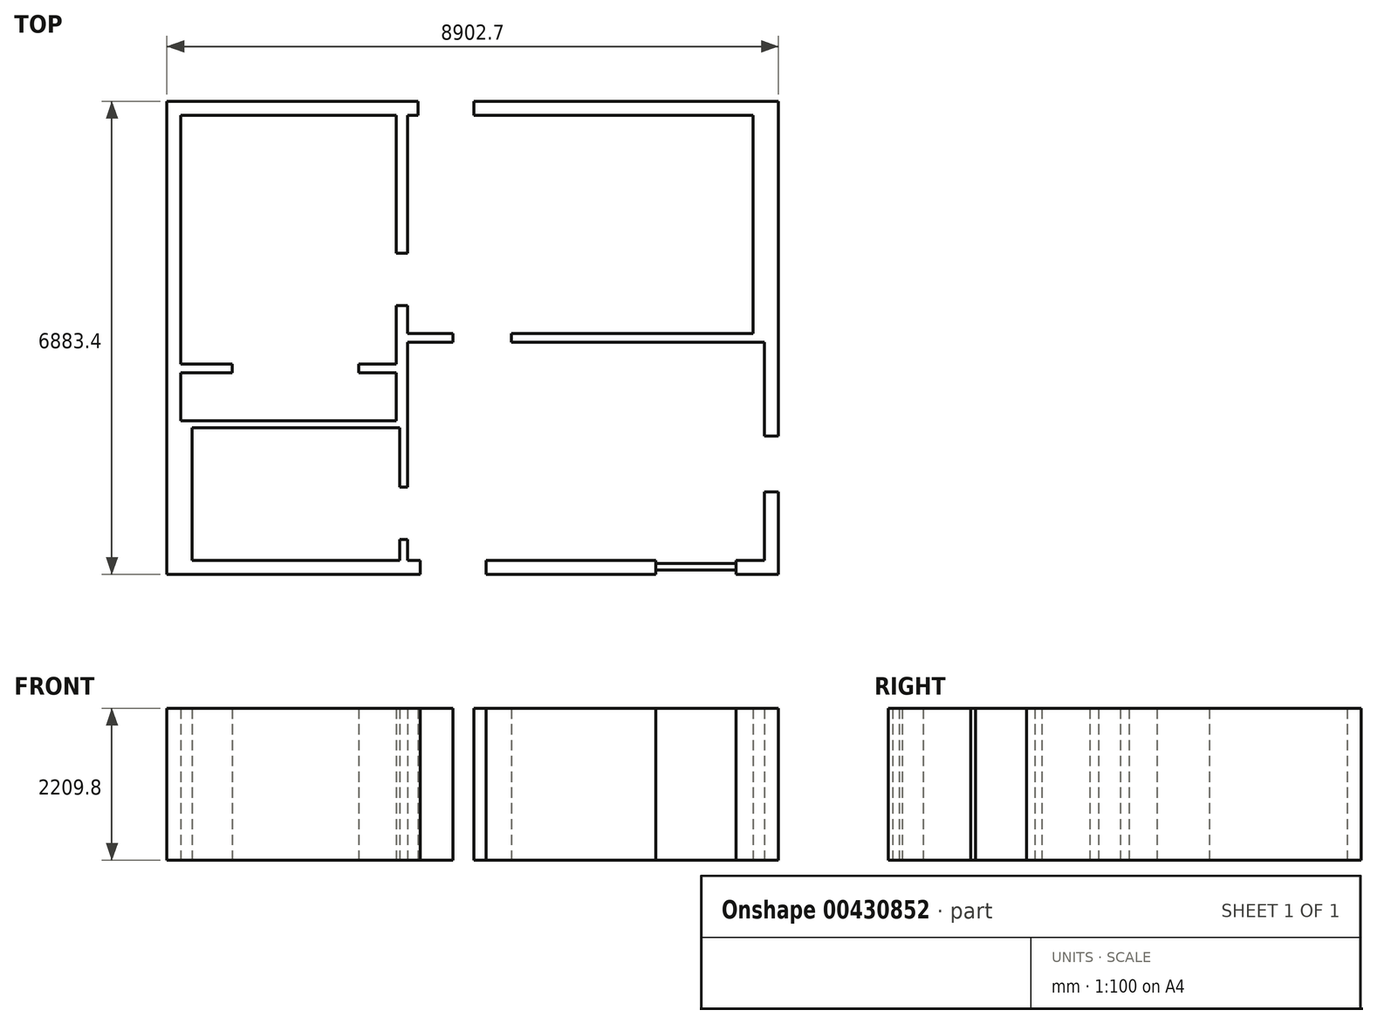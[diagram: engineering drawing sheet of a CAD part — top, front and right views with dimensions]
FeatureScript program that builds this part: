
annotation { "Feature Type Name" : "Feature", "Feature Type Description" : "" }
export const myFeature = defineFeature(function(context is Context, id is Id, definition is map)
    precondition{}
    {
        {
            var Q0;
            Q0=qCreatedBy(makeId("Top.planeOp"),FACE);
            var sketch = newSketch(context, id + "F0", { "sketchPlane" : qUnion([Q0])});
            skLineSegment(sketch, "E0.bottom", {"start": v(-727.6, 2739) * mm, "end": v(-575.2, 2739) * mm});
            skLineSegment(sketch, "E0.top", {"start": v(-727.6, -436) * mm, "end": v(-67.2, -436) * mm});
            skLineSegment(sketch, "E0.left", {"start": v(-727.6, 2739) * mm, "end": v(-727.6, 732.4) * mm});
            skLineSegment(sketch, "E0.right", {"start": v(4301.6, 2739) * mm, "end": v(4301.6, -436) * mm});
            skLineSegment(sketch, "E1.bottom", {"start": v(-727.6, -563) * mm, "end": v(-67.2, -563) * mm});
            skLineSegment(sketch, "E1.top", {"start": v(-727.6, -3738) * mm, "end": v(-546.63, -3738) * mm});
            skLineSegment(sketch, "E1.left", {"start": v(-727.6, -563) * mm, "end": v(-727.6, -2671.2) * mm});
            skLineSegment(sketch, "E1.right", {"start": v(4466.7, -563) * mm, "end": v(4466.7, -1928.26) * mm});
            skLineSegment(sketch, "E2.bottom", {"start": v(-4029.6, -880.5) * mm, "end": v(-3280.3, -880.5) * mm});
            skLineSegment(sketch, "E2.top", {"start": v(-4029.6, 2739) * mm, "end": v(-892.7, 2739) * mm});
            skLineSegment(sketch, "E2.left", {"start": v(-4029.6, -880.5) * mm, "end": v(-4029.6, 2739) * mm});
            skLineSegment(sketch, "E2.right", {"start": v(-892.7, -880.5) * mm, "end": v(-892.7, -29.6) * mm});
            skLineSegment(sketch, "E3.bottom", {"start": v(-3864.5, -1807.6) * mm, "end": v(-841.9, -1807.6) * mm});
            skLineSegment(sketch, "E3.top", {"start": v(-3864.5, -3738) * mm, "end": v(-841.9, -3738) * mm});
            skLineSegment(sketch, "E3.left", {"start": v(-3864.5, -1807.6) * mm, "end": v(-3864.5, -3738) * mm});
            skLineSegment(sketch, "E3.right", {"start": v(-841.9, -1807.6) * mm, "end": v(-841.9, -2671.2) * mm});
            skLineSegment(sketch, "E4", {"start": v(-67.2, -563) * mm, "end": v(-67.2, -436) * mm});
            skLineSegment(sketch, "E5.bottom", {"start": v(-4029.6, -1007.5) * mm, "end": v(-3280.3, -1007.5) * mm});
            skLineSegment(sketch, "E5.top", {"start": v(-4029.6, -1706) * mm, "end": v(-892.7, -1706) * mm});
            skLineSegment(sketch, "E5.left", {"start": v(-4029.6, -1007.5) * mm, "end": v(-4029.6, -1706) * mm});
            skLineSegment(sketch, "E5.right", {"start": v(-892.7, -1007.5) * mm, "end": v(-892.7, -1706) * mm});
            skLineSegment(sketch, "E6", {"start": v(-3280.3, -1007.5) * mm, "end": v(-3280.3, -880.5) * mm});
            skLineSegment(sketch, "E7", {"start": v(-1438.8, -1007.5) * mm, "end": v(-1438.8, -880.5) * mm});
            skLineSegment(sketch, "E8.trimOffspring", {"start": v(-1438.8, -880.5) * mm, "end": v(-892.7, -880.5) * mm});
            skLineSegment(sketch, "E9.trimOffspring", {"start": v(-1438.8, -1007.5) * mm, "end": v(-892.7, -1007.5) * mm});
            skLineSegment(sketch, "E10", {"start": v(783.7, -563) * mm, "end": v(783.7, -436) * mm});
            skLineSegment(sketch, "E11.trimOffspring", {"start": v(783.7, -563) * mm, "end": v(4466.7, -563) * mm});
            skLineSegment(sketch, "E12.trimOffspring", {"start": v(783.7, -436) * mm, "end": v(4301.6, -436) * mm});
            skLineSegment(sketch, "E13", {"start": v(415.4, -3738) * mm, "end": v(415.4, -3941.2) * mm});
            skLineSegment(sketch, "E14", {"start": v(-546.63, -3941.2) * mm, "end": v(-546.63, -3738) * mm});
            skLineSegment(sketch, "E15.bottom", {"start": v(-4232.8, 2942.2) * mm, "end": v(-575.2, 2942.2) * mm});
            skLineSegment(sketch, "E15.top", {"start": v(-4232.8, -3941.2) * mm, "end": v(-546.63, -3941.2) * mm});
            skLineSegment(sketch, "E15.left", {"start": v(-4232.8, 2942.2) * mm, "end": v(-4232.8, -3941.2) * mm});
            skLineSegment(sketch, "E15.right", {"start": v(4669.9, 2942.2) * mm, "end": v(4669.9, -1928.26) * mm});
            skLineSegment(sketch, "E16.trimOffspring", {"start": v(415.4, -3941.2) * mm, "end": v(2885.55, -3941.2) * mm});
            skLineSegment(sketch, "E17.trimOffspring", {"start": v(415.4, -3738) * mm, "end": v(2885.55, -3738) * mm});
            skLineSegment(sketch, "E18", {"start": v(-892.7, -29.6) * mm, "end": v(-727.6, -29.6) * mm});
            skLineSegment(sketch, "E19", {"start": v(-727.6, 732.4) * mm, "end": v(-892.7, 732.4) * mm});
            skLineSegment(sketch, "E20.trimOffspring", {"start": v(-892.7, 732.4) * mm, "end": v(-892.7, 2739) * mm});
            skLineSegment(sketch, "E21.trimOffspring", {"start": v(-727.6, -29.6) * mm, "end": v(-727.6, -436) * mm});
            skLineSegment(sketch, "E22", {"start": v(-841.9, -3433.2) * mm, "end": v(-727.6, -3433.2) * mm});
            skLineSegment(sketch, "E23", {"start": v(-727.6, -2671.2) * mm, "end": v(-841.9, -2671.2) * mm});
            skLineSegment(sketch, "E24.trimOffspring", {"start": v(-727.6, -3433.2) * mm, "end": v(-727.6, -3738) * mm});
            skLineSegment(sketch, "E25.trimOffspring", {"start": v(-841.9, -3433.2) * mm, "end": v(-841.9, -3738) * mm});
            skLineSegment(sketch, "E26", {"start": v(4466.7, -2741.06) * mm, "end": v(4669.9, -2741.06) * mm});
            skLineSegment(sketch, "E27", {"start": v(4669.9, -1928.26) * mm, "end": v(4466.7, -1928.26) * mm});
            skLineSegment(sketch, "E28.trimOffspring", {"start": v(4669.9, -2741.06) * mm, "end": v(4669.9, -3941.2) * mm});
            skLineSegment(sketch, "E29.trimOffspring", {"start": v(4466.7, -2741.06) * mm, "end": v(4466.7, -3738) * mm});
            skLineSegment(sketch, "E30", {"start": v(-575.2, 2739) * mm, "end": v(-575.2, 2942.2) * mm});
            skLineSegment(sketch, "E31", {"start": v(237.6, 2942.2) * mm, "end": v(237.6, 2739) * mm});
            skLineSegment(sketch, "E32.trimOffspring", {"start": v(237.6, 2739) * mm, "end": v(4301.6, 2739) * mm});
            skLineSegment(sketch, "E33.trimOffspring", {"start": v(237.6, 2942.2) * mm, "end": v(4669.9, 2942.2) * mm});
            skLineSegment(sketch, "E34", {"start": v(2885.55, -3941.2) * mm, "end": v(2885.55, -3738) * mm});
            skLineSegment(sketch, "E35", {"start": v(4053.95, -3738) * mm, "end": v(4053.95, -3941.2) * mm});
            skLineSegment(sketch, "E36.trimOffspring", {"start": v(4053.95, -3941.2) * mm, "end": v(4669.9, -3941.2) * mm});
            skLineSegment(sketch, "E37.trimOffspring", {"start": v(4053.95, -3738) * mm, "end": v(4466.7, -3738) * mm});
            skLineSegment(sketch, "E38.bottom", {"start": v(2885.55, -3784.8) * mm, "end": v(4053.95, -3784.8) * mm});
            skLineSegment(sketch, "E38.top", {"start": v(2885.55, -3880.17) * mm, "end": v(4053.95, -3880.17) * mm});
            skLineSegment(sketch, "E38.left", {"start": v(2885.55, -3784.8) * mm, "end": v(2885.55, -3880.17) * mm});
            skLineSegment(sketch, "E38.right", {"start": v(4053.95, -3784.8) * mm, "end": v(4053.95, -3880.17) * mm});
            skSolve(sketch);
        }
        {
            var Q0;
            Q0=makeQuery(id+"F0.imprint","IMPRINT",FACE,{"disambiguationData":[TD([[makeQuery(id+"F0.imprint","IMPRINT",EDGE,{"derivedFrom":sQuery(id+"F0.wireOp",EDGE,"E0.bottom")}),1.0]])]});
            var Q1;
            Q1=makeQuery(id+"F0.imprint","IMPRINT",FACE,{"disambiguationData":[TD([[makeQuery(id+"F0.imprint","IMPRINT",EDGE,{"derivedFrom":sQuery(id+"F0.wireOp",EDGE,"E13")}),1.0]])]});
            var Q2;
            Q2=makeQuery(id+"F0.imprint","IMPRINT",FACE,{"disambiguationData":[TD([[makeQuery(id+"F0.imprint","IMPRINT",EDGE,{"derivedFrom":sQuery(id+"F0.wireOp",EDGE,"E26")}),-1.0]])]});
            var Q3;
            Q3=makeQuery(id+"F0.imprint","IMPRINT",FACE,{"disambiguationData":[TD([[makeQuery(id+"F0.imprint","IMPRINT",EDGE,{"derivedFrom":sQuery(id+"F0.wireOp",EDGE,"E0.right")}),1.0]])]});
            extrude(context, id + "F1", {"entities" : qUnion([Q0, Q1, Q2, Q3]), "depth" : 2209.8 * mm});
        }
        {
            var Q0;
            Q0=makeQuery(id+"F0.imprint","IMPRINT",FACE,{"disambiguationData":[TD([[makeQuery(id+"F0.imprint","IMPRINT",EDGE,{"derivedFrom":sQuery(id+"F0.wireOp",EDGE,"E38.bottom")}),-1.0]])]});
            var Q1;
            Q1=makeQuery(id+"F1.opExtrude","CAP_FACE",FACE,{"disambiguationData":[OSD([sQuery(id+"F0.wireOp",EDGE,"E26"),sQuery(id+"F0.wireOp",EDGE,"E28.trimOffspring"),sQuery(id+"F0.wireOp",EDGE,"E29.trimOffspring"),sQuery(id+"F0.wireOp",EDGE,"E35"),sQuery(id+"F0.wireOp",EDGE,"E36.trimOffspring"),sQuery(id+"F0.wireOp",EDGE,"E37.trimOffspring"),sQuery(id+"F0.wireOp",EDGE,"E38.right")])],"isStart":false});
            var Q2;
            Q2=makeQuery(id+"F1.opExtrude","CAP_FACE",FACE,{"disambiguationData":[OSD([sQuery(id+"F0.wireOp",EDGE,"E26"),sQuery(id+"F0.wireOp",EDGE,"E28.trimOffspring"),sQuery(id+"F0.wireOp",EDGE,"E29.trimOffspring"),sQuery(id+"F0.wireOp",EDGE,"E35"),sQuery(id+"F0.wireOp",EDGE,"E36.trimOffspring"),sQuery(id+"F0.wireOp",EDGE,"E37.trimOffspring"),sQuery(id+"F0.wireOp",EDGE,"E38.right")])],"isStart":false});
            extrude(context, id + "F2", {"entities" : qUnion([Q0]), "endBound" : BoundingType.UP_TO_SURFACE, "endBoundEntityFace" : qUnion([Q1]), "depth" : 25.4 * mm});
        }
    });
